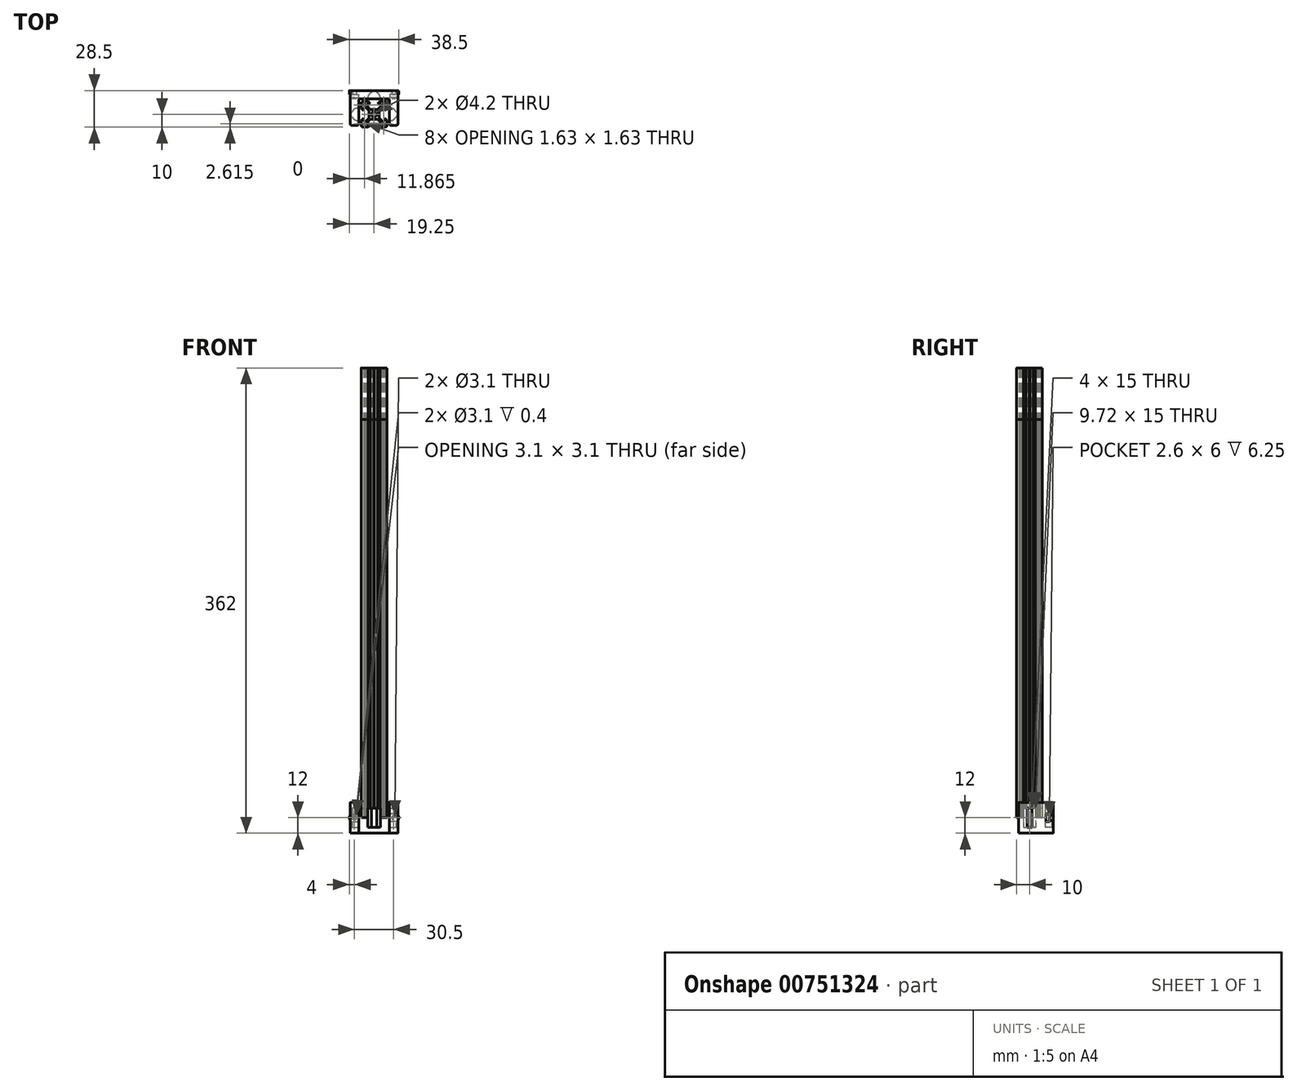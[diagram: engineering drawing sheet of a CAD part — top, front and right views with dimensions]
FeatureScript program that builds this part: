
annotation { "Feature Type Name" : "Feature", "Feature Type Description" : "" }
export const myFeature = defineFeature(function(context is Context, id is Id, definition is map)
    precondition{}
    {
        {
            var Q0;
            Q0=qCreatedBy(makeId("Top.planeOp"),FACE);
            var sketch = newSketch(context, id + "F0", { "sketchPlane" : qUnion([Q0])});
            skArc(sketch, "E0", {"start": v(-8.5, 10) * mm, "mid": v(-9.56, 9.56) * mm, "end": v(-10, 8.5) * mm});
            skLineSegment(sketch, "E1", {"start": v(-10, 8.5) * mm, "end": v(-10, 4.64) * mm});
            skLineSegment(sketch, "E2", {"start": v(-10, 4.64) * mm, "end": v(-8.2, 2.84) * mm});
            skLineSegment(sketch, "E3", {"start": v(-8.2, 5.5) * mm, "end": v(-8.2, 2.84) * mm});
            skLineSegment(sketch, "E4", {"start": v(-8.2, 5.5) * mm, "end": v(-6.56, 5.5) * mm});
            skLineSegment(sketch, "E5", {"start": v(-6.56, 5.5) * mm, "end": v(-3.9, 2.84) * mm});
            skLineSegment(sketch, "E6", {"start": v(-3.9, 2.84) * mm, "end": v(-3.9, 0.2) * mm});
            skLineSegment(sketch, "E7", {"start": v(-3.9, 0.2) * mm, "end": v(-3.7, 0) * mm});
            skLineSegment(sketch, "E8", {"start": v(-3.9, -0.2) * mm, "end": v(-3.7, 0) * mm});
            skLineSegment(sketch, "E9", {"start": v(-3.9, -2.84) * mm, "end": v(-3.9, -0.2) * mm});
            skLineSegment(sketch, "E10", {"start": v(-6.56, -5.5) * mm, "end": v(-3.9, -2.84) * mm});
            skLineSegment(sketch, "E11", {"start": v(-8.2, -5.5) * mm, "end": v(-6.56, -5.5) * mm});
            skLineSegment(sketch, "E12", {"start": v(-8.2, -5.5) * mm, "end": v(-8.2, -2.84) * mm});
            skLineSegment(sketch, "E13", {"start": v(-10, -4.64) * mm, "end": v(-8.2, -2.84) * mm});
            skLineSegment(sketch, "E14", {"start": v(-10, -8.5) * mm, "end": v(-10, -4.64) * mm});
            skArc(sketch, "E15", {"start": v(-10, -8.5) * mm, "mid": v(-9.56, -9.56) * mm, "end": v(-8.5, -10) * mm});
            skLineSegment(sketch, "E16", {"start": v(-8.5, -10) * mm, "end": v(-4.64, -10) * mm});
            skLineSegment(sketch, "E17", {"start": v(-4.64, -10) * mm, "end": v(-2.84, -8.2) * mm});
            skLineSegment(sketch, "E18", {"start": v(-2.84, -8.2) * mm, "end": v(-5.5, -8.2) * mm});
            skLineSegment(sketch, "E19", {"start": v(-5.5, -8.2) * mm, "end": v(-5.5, -6.56) * mm});
            skLineSegment(sketch, "E20", {"start": v(-5.5, -6.56) * mm, "end": v(-2.84, -3.9) * mm});
            skLineSegment(sketch, "E21", {"start": v(-0.2, -3.9) * mm, "end": v(-2.84, -3.9) * mm});
            skLineSegment(sketch, "E22", {"start": v(-0.2, -3.9) * mm, "end": v(0, -3.7) * mm});
            skLineSegment(sketch, "E23", {"start": v(0.2, -3.9) * mm, "end": v(0, -3.7) * mm});
            skLineSegment(sketch, "E24", {"start": v(0.2, -3.9) * mm, "end": v(2.84, -3.9) * mm});
            skLineSegment(sketch, "E25", {"start": v(5.5, -6.56) * mm, "end": v(2.84, -3.9) * mm});
            skLineSegment(sketch, "E26", {"start": v(5.5, -8.2) * mm, "end": v(5.5, -6.56) * mm});
            skLineSegment(sketch, "E27", {"start": v(2.84, -8.2) * mm, "end": v(5.5, -8.2) * mm});
            skLineSegment(sketch, "E28", {"start": v(4.64, -10) * mm, "end": v(2.84, -8.2) * mm});
            skLineSegment(sketch, "E29", {"start": v(8.5, -10) * mm, "end": v(4.64, -10) * mm});
            skArc(sketch, "E30", {"start": v(8.5, -10) * mm, "mid": v(9.56, -9.56) * mm, "end": v(10, -8.5) * mm});
            skLineSegment(sketch, "E31", {"start": v(10, -8.5) * mm, "end": v(10, -4.64) * mm});
            skLineSegment(sketch, "E32", {"start": v(10, -4.64) * mm, "end": v(8.2, -2.84) * mm});
            skLineSegment(sketch, "E33", {"start": v(8.2, -5.5) * mm, "end": v(8.2, -2.84) * mm});
            skLineSegment(sketch, "E34", {"start": v(8.2, -5.5) * mm, "end": v(6.56, -5.5) * mm});
            skLineSegment(sketch, "E35", {"start": v(6.56, -5.5) * mm, "end": v(3.9, -2.84) * mm});
            skLineSegment(sketch, "E36", {"start": v(3.9, -2.84) * mm, "end": v(3.9, -0.2) * mm});
            skLineSegment(sketch, "E37", {"start": v(3.9, -0.2) * mm, "end": v(3.7, 0) * mm});
            skLineSegment(sketch, "E38", {"start": v(3.9, 0.2) * mm, "end": v(3.7, 0) * mm});
            skLineSegment(sketch, "E39", {"start": v(3.9, 2.84) * mm, "end": v(3.9, 0.2) * mm});
            skLineSegment(sketch, "E40", {"start": v(6.56, 5.5) * mm, "end": v(3.9, 2.84) * mm});
            skLineSegment(sketch, "E41", {"start": v(8.2, 5.5) * mm, "end": v(6.56, 5.5) * mm});
            skLineSegment(sketch, "E42", {"start": v(8.2, 5.5) * mm, "end": v(8.2, 2.84) * mm});
            skLineSegment(sketch, "E43", {"start": v(10, 4.64) * mm, "end": v(8.2, 2.84) * mm});
            skLineSegment(sketch, "E44", {"start": v(10, 8.5) * mm, "end": v(10, 4.64) * mm});
            skArc(sketch, "E45", {"start": v(10, 8.5) * mm, "mid": v(9.56, 9.56) * mm, "end": v(8.5, 10) * mm});
            skLineSegment(sketch, "E46", {"start": v(8.5, 10) * mm, "end": v(4.64, 10) * mm});
            skLineSegment(sketch, "E47", {"start": v(4.64, 10) * mm, "end": v(2.84, 8.2) * mm});
            skLineSegment(sketch, "E48", {"start": v(2.84, 8.2) * mm, "end": v(5.5, 8.2) * mm});
            skLineSegment(sketch, "E49", {"start": v(5.5, 8.2) * mm, "end": v(5.5, 6.56) * mm});
            skLineSegment(sketch, "E50", {"start": v(5.5, 6.56) * mm, "end": v(2.84, 3.9) * mm});
            skLineSegment(sketch, "E51", {"start": v(0.2, 3.9) * mm, "end": v(2.84, 3.9) * mm});
            skLineSegment(sketch, "E52", {"start": v(0.2, 3.9) * mm, "end": v(0, 3.7) * mm});
            skLineSegment(sketch, "E53", {"start": v(-0.2, 3.9) * mm, "end": v(0, 3.7) * mm});
            skLineSegment(sketch, "E54", {"start": v(-0.2, 3.9) * mm, "end": v(-2.84, 3.9) * mm});
            skLineSegment(sketch, "E55", {"start": v(-5.5, 6.56) * mm, "end": v(-2.84, 3.9) * mm});
            skLineSegment(sketch, "E56", {"start": v(-5.5, 8.2) * mm, "end": v(-5.5, 6.56) * mm});
            skLineSegment(sketch, "E57", {"start": v(-2.84, 8.2) * mm, "end": v(-5.5, 8.2) * mm});
            skLineSegment(sketch, "E58", {"start": v(-4.64, 10) * mm, "end": v(-2.84, 8.2) * mm});
            skLineSegment(sketch, "E59", {"start": v(-8.5, 10) * mm, "end": v(-4.64, 10) * mm});
            skCircle(sketch, "E60", {"center": v(0, 0) * mm, "radius": 2.1 * mm});
            skLineSegment(sketch, "E61", {"start": v(-6.57, 8.2) * mm, "end": v(-8.2, 8.2) * mm});
            skLineSegment(sketch, "E62", {"start": v(-6.57, 8.2) * mm, "end": v(-6.57, 7.63) * mm});
            skLineSegment(sketch, "E63", {"start": v(-7.63, 6.57) * mm, "end": v(-6.57, 7.63) * mm});
            skLineSegment(sketch, "E64", {"start": v(-8.2, 6.57) * mm, "end": v(-7.63, 6.57) * mm});
            skLineSegment(sketch, "E65", {"start": v(-8.2, 8.2) * mm, "end": v(-8.2, 6.57) * mm});
            skLineSegment(sketch, "E66", {"start": v(8.2, 8.2) * mm, "end": v(8.2, 6.57) * mm});
            skLineSegment(sketch, "E67", {"start": v(8.2, 6.57) * mm, "end": v(7.63, 6.57) * mm});
            skLineSegment(sketch, "E68", {"start": v(7.63, 6.57) * mm, "end": v(6.57, 7.63) * mm});
            skLineSegment(sketch, "E69", {"start": v(6.57, 8.2) * mm, "end": v(6.57, 7.63) * mm});
            skLineSegment(sketch, "E70", {"start": v(6.57, 8.2) * mm, "end": v(8.2, 8.2) * mm});
            skLineSegment(sketch, "E71", {"start": v(-8.2, -8.2) * mm, "end": v(-8.2, -6.57) * mm});
            skLineSegment(sketch, "E72", {"start": v(-8.2, -6.57) * mm, "end": v(-7.63, -6.57) * mm});
            skLineSegment(sketch, "E73", {"start": v(-7.63, -6.57) * mm, "end": v(-6.57, -7.63) * mm});
            skLineSegment(sketch, "E74", {"start": v(-6.57, -8.2) * mm, "end": v(-6.57, -7.63) * mm});
            skLineSegment(sketch, "E75", {"start": v(-6.57, -8.2) * mm, "end": v(-8.2, -8.2) * mm});
            skLineSegment(sketch, "E76", {"start": v(6.57, -8.2) * mm, "end": v(8.2, -8.2) * mm});
            skLineSegment(sketch, "E77", {"start": v(6.57, -8.2) * mm, "end": v(6.57, -7.63) * mm});
            skLineSegment(sketch, "E78", {"start": v(7.63, -6.57) * mm, "end": v(6.57, -7.63) * mm});
            skLineSegment(sketch, "E79", {"start": v(8.2, -6.57) * mm, "end": v(7.63, -6.57) * mm});
            skLineSegment(sketch, "E80", {"start": v(8.2, -8.2) * mm, "end": v(8.2, -6.57) * mm});
            skSolve(sketch);
        }
        {
            var Q0;
            Q0 = qSketchRegion(id + "F0", true);
            extrude(context, id + "F1", {"entities" : qUnion([Q0]), "depth" : 310 * mm, "offsetDistance" : 25 * mm});
        }
        {
            var Q0;
            Q0 = qSketchRegion(id + "F0", true);
            extrude(context, id + "F2", {"entities" : qUnion([Q0]), "depth" : 350 * mm, "offsetDistance" : 25 * mm});
        }
        {
            var Q0;
            Q0=qCreatedBy(makeId("Top.planeOp"),FACE);
            var sketch = newSketch(context, id + "F3", { "sketchPlane" : qUnion([Q0])});
            skLineSegment(sketch, "E81.0.0", {"start": v(-4.64, 10) * mm, "end": v(-8.5, 10) * mm, "construction": true});
            skArc(sketch, "E81.0.1", {"start": v(-8.5, 10) * mm, "mid": v(-9.56, 9.56) * mm, "end": v(-10, 8.5) * mm, "construction": true});
            skLineSegment(sketch, "E81.0.2", {"start": v(-10, 8.5) * mm, "end": v(-10, 4.64) * mm, "construction": true});
            skLineSegment(sketch, "E81.0.3", {"start": v(-10, 4.64) * mm, "end": v(-8.2, 2.84) * mm, "construction": true});
            skLineSegment(sketch, "E81.0.4", {"start": v(-8.2, 2.84) * mm, "end": v(-8.2, 5.5) * mm, "construction": true});
            skLineSegment(sketch, "E81.0.5", {"start": v(-8.2, 5.5) * mm, "end": v(-6.56, 5.5) * mm, "construction": true});
            skLineSegment(sketch, "E81.0.6", {"start": v(-6.56, 5.5) * mm, "end": v(-3.9, 2.84) * mm, "construction": true});
            skLineSegment(sketch, "E81.0.7", {"start": v(-3.9, 2.84) * mm, "end": v(-3.9, 0.2) * mm, "construction": true});
            skLineSegment(sketch, "E81.0.8", {"start": v(-3.9, 0.2) * mm, "end": v(-3.7, 0) * mm, "construction": true});
            skLineSegment(sketch, "E81.0.9", {"start": v(-3.7, 0) * mm, "end": v(-3.9, -0.2) * mm, "construction": true});
            skLineSegment(sketch, "E81.0.10", {"start": v(-3.9, -0.2) * mm, "end": v(-3.9, -2.84) * mm, "construction": true});
            skLineSegment(sketch, "E81.0.11", {"start": v(-3.9, -2.84) * mm, "end": v(-6.56, -5.5) * mm, "construction": true});
            skLineSegment(sketch, "E81.0.12", {"start": v(-6.56, -5.5) * mm, "end": v(-8.2, -5.5) * mm, "construction": true});
            skLineSegment(sketch, "E81.0.13", {"start": v(-8.2, -5.5) * mm, "end": v(-8.2, -2.84) * mm, "construction": true});
            skLineSegment(sketch, "E81.0.14", {"start": v(-8.2, -2.84) * mm, "end": v(-10, -4.64) * mm, "construction": true});
            skLineSegment(sketch, "E81.0.15", {"start": v(-10, -4.64) * mm, "end": v(-10, -8.5) * mm, "construction": true});
            skArc(sketch, "E81.0.16", {"start": v(-10, -8.5) * mm, "mid": v(-9.56, -9.56) * mm, "end": v(-8.5, -10) * mm, "construction": true});
            skLineSegment(sketch, "E81.0.17", {"start": v(-8.5, -10) * mm, "end": v(-4.64, -10) * mm, "construction": true});
            skLineSegment(sketch, "E81.0.18", {"start": v(-4.64, -10) * mm, "end": v(-2.84, -8.2) * mm, "construction": true});
            skLineSegment(sketch, "E81.0.19", {"start": v(-2.84, -8.2) * mm, "end": v(-5.5, -8.2) * mm, "construction": true});
            skLineSegment(sketch, "E81.0.20", {"start": v(-5.5, -8.2) * mm, "end": v(-5.5, -6.56) * mm, "construction": true});
            skLineSegment(sketch, "E81.0.21", {"start": v(-5.5, -6.56) * mm, "end": v(-2.84, -3.9) * mm, "construction": true});
            skLineSegment(sketch, "E81.0.22", {"start": v(-2.84, -3.9) * mm, "end": v(-0.2, -3.9) * mm, "construction": true});
            skLineSegment(sketch, "E81.0.23", {"start": v(-0.2, -3.9) * mm, "end": v(0, -3.7) * mm, "construction": true});
            skLineSegment(sketch, "E81.0.24", {"start": v(0, -3.7) * mm, "end": v(0.2, -3.9) * mm, "construction": true});
            skLineSegment(sketch, "E81.0.25", {"start": v(0.2, -3.9) * mm, "end": v(2.84, -3.9) * mm, "construction": true});
            skLineSegment(sketch, "E81.0.26", {"start": v(2.84, -3.9) * mm, "end": v(5.5, -6.56) * mm, "construction": true});
            skLineSegment(sketch, "E81.0.27", {"start": v(5.5, -6.56) * mm, "end": v(5.5, -8.2) * mm, "construction": true});
            skLineSegment(sketch, "E81.0.28", {"start": v(5.5, -8.2) * mm, "end": v(2.84, -8.2) * mm, "construction": true});
            skLineSegment(sketch, "E81.0.29", {"start": v(2.84, -8.2) * mm, "end": v(4.64, -10) * mm, "construction": true});
            skLineSegment(sketch, "E81.0.30", {"start": v(4.64, -10) * mm, "end": v(8.5, -10) * mm, "construction": true});
            skArc(sketch, "E81.0.31", {"start": v(8.5, -10) * mm, "mid": v(9.56, -9.56) * mm, "end": v(10, -8.5) * mm, "construction": true});
            skLineSegment(sketch, "E81.0.32", {"start": v(10, -8.5) * mm, "end": v(10, -4.64) * mm, "construction": true});
            skLineSegment(sketch, "E81.0.33", {"start": v(10, -4.64) * mm, "end": v(8.2, -2.84) * mm, "construction": true});
            skLineSegment(sketch, "E81.0.34", {"start": v(8.2, -2.84) * mm, "end": v(8.2, -5.5) * mm, "construction": true});
            skLineSegment(sketch, "E81.0.35", {"start": v(8.2, -5.5) * mm, "end": v(6.56, -5.5) * mm, "construction": true});
            skLineSegment(sketch, "E81.0.36", {"start": v(6.56, -5.5) * mm, "end": v(3.9, -2.84) * mm, "construction": true});
            skLineSegment(sketch, "E81.0.37", {"start": v(3.9, -2.84) * mm, "end": v(3.9, -0.2) * mm, "construction": true});
            skLineSegment(sketch, "E81.0.38", {"start": v(3.9, -0.2) * mm, "end": v(3.7, 0) * mm, "construction": true});
            skLineSegment(sketch, "E81.0.39", {"start": v(3.7, 0) * mm, "end": v(3.9, 0.2) * mm, "construction": true});
            skLineSegment(sketch, "E81.0.40", {"start": v(3.9, 0.2) * mm, "end": v(3.9, 2.84) * mm, "construction": true});
            skLineSegment(sketch, "E81.0.41", {"start": v(3.9, 2.84) * mm, "end": v(6.56, 5.5) * mm, "construction": true});
            skLineSegment(sketch, "E81.0.42", {"start": v(6.56, 5.5) * mm, "end": v(8.2, 5.5) * mm, "construction": true});
            skLineSegment(sketch, "E81.0.43", {"start": v(8.2, 5.5) * mm, "end": v(8.2, 2.84) * mm, "construction": true});
            skLineSegment(sketch, "E81.0.44", {"start": v(8.2, 2.84) * mm, "end": v(10, 4.64) * mm, "construction": true});
            skLineSegment(sketch, "E81.0.45", {"start": v(10, 4.64) * mm, "end": v(10, 8.5) * mm, "construction": true});
            skArc(sketch, "E81.0.46", {"start": v(10, 8.5) * mm, "mid": v(9.56, 9.56) * mm, "end": v(8.5, 10) * mm, "construction": true});
            skLineSegment(sketch, "E81.0.47", {"start": v(8.5, 10) * mm, "end": v(4.64, 10) * mm, "construction": true});
            skLineSegment(sketch, "E81.0.48", {"start": v(4.64, 10) * mm, "end": v(2.84, 8.2) * mm, "construction": true});
            skLineSegment(sketch, "E81.0.49", {"start": v(2.84, 8.2) * mm, "end": v(5.5, 8.2) * mm, "construction": true});
            skLineSegment(sketch, "E81.0.50", {"start": v(5.5, 8.2) * mm, "end": v(5.5, 6.56) * mm, "construction": true});
            skLineSegment(sketch, "E81.0.51", {"start": v(5.5, 6.56) * mm, "end": v(2.84, 3.9) * mm, "construction": true});
            skLineSegment(sketch, "E81.0.52", {"start": v(2.84, 3.9) * mm, "end": v(0.2, 3.9) * mm, "construction": true});
            skLineSegment(sketch, "E81.0.53", {"start": v(0.2, 3.9) * mm, "end": v(0, 3.7) * mm, "construction": true});
            skLineSegment(sketch, "E81.0.54", {"start": v(0, 3.7) * mm, "end": v(-0.2, 3.9) * mm, "construction": true});
            skLineSegment(sketch, "E81.0.55", {"start": v(-0.2, 3.9) * mm, "end": v(-2.84, 3.9) * mm, "construction": true});
            skLineSegment(sketch, "E81.0.56", {"start": v(-2.84, 3.9) * mm, "end": v(-5.5, 6.56) * mm, "construction": true});
            skLineSegment(sketch, "E81.0.57", {"start": v(-5.5, 6.56) * mm, "end": v(-5.5, 8.2) * mm, "construction": true});
            skLineSegment(sketch, "E81.0.58", {"start": v(-5.5, 8.2) * mm, "end": v(-2.84, 8.2) * mm, "construction": true});
            skLineSegment(sketch, "E81.0.59", {"start": v(-2.84, 8.2) * mm, "end": v(-4.64, 10) * mm, "construction": true});
            skLineSegment(sketch, "E82.0.0", {"start": v(-6.57, 8.2) * mm, "end": v(-8.2, 8.2) * mm, "construction": true});
            skLineSegment(sketch, "E82.0.1", {"start": v(-8.2, 8.2) * mm, "end": v(-8.2, 6.57) * mm, "construction": true});
            skLineSegment(sketch, "E82.0.2", {"start": v(-8.2, 6.57) * mm, "end": v(-7.63, 6.57) * mm, "construction": true});
            skLineSegment(sketch, "E82.0.3", {"start": v(-7.63, 6.57) * mm, "end": v(-6.57, 7.63) * mm, "construction": true});
            skLineSegment(sketch, "E82.0.4", {"start": v(-6.57, 7.63) * mm, "end": v(-6.57, 8.2) * mm, "construction": true});
            skLineSegment(sketch, "E83.0.0", {"start": v(8.2, 8.2) * mm, "end": v(6.57, 8.2) * mm, "construction": true});
            skLineSegment(sketch, "E83.0.1", {"start": v(6.57, 8.2) * mm, "end": v(6.57, 7.63) * mm, "construction": true});
            skLineSegment(sketch, "E83.0.2", {"start": v(6.57, 7.63) * mm, "end": v(7.63, 6.57) * mm, "construction": true});
            skLineSegment(sketch, "E83.0.3", {"start": v(7.63, 6.57) * mm, "end": v(8.2, 6.57) * mm, "construction": true});
            skLineSegment(sketch, "E83.0.4", {"start": v(8.2, 6.57) * mm, "end": v(8.2, 8.2) * mm, "construction": true});
            skLineSegment(sketch, "E84.0.0", {"start": v(-8.2, -8.2) * mm, "end": v(-6.57, -8.2) * mm, "construction": true});
            skLineSegment(sketch, "E84.0.1", {"start": v(-6.57, -8.2) * mm, "end": v(-6.57, -7.63) * mm, "construction": true});
            skLineSegment(sketch, "E84.0.2", {"start": v(-6.57, -7.63) * mm, "end": v(-7.63, -6.57) * mm, "construction": true});
            skLineSegment(sketch, "E84.0.3", {"start": v(-7.63, -6.57) * mm, "end": v(-8.2, -6.57) * mm, "construction": true});
            skLineSegment(sketch, "E84.0.4", {"start": v(-8.2, -6.57) * mm, "end": v(-8.2, -8.2) * mm, "construction": true});
            skLineSegment(sketch, "E85.0.0", {"start": v(6.57, -8.2) * mm, "end": v(8.2, -8.2) * mm, "construction": true});
            skLineSegment(sketch, "E85.0.1", {"start": v(8.2, -8.2) * mm, "end": v(8.2, -6.57) * mm, "construction": true});
            skLineSegment(sketch, "E85.0.2", {"start": v(8.2, -6.57) * mm, "end": v(7.63, -6.57) * mm, "construction": true});
            skLineSegment(sketch, "E85.0.3", {"start": v(7.63, -6.57) * mm, "end": v(6.57, -7.63) * mm, "construction": true});
            skLineSegment(sketch, "E85.0.4", {"start": v(6.57, -7.63) * mm, "end": v(6.57, -8.2) * mm, "construction": true});
            skCircle(sketch, "E86.0", {"center": v(0, 0) * mm, "radius": 2.1 * mm, "construction": true});
            skCircle(sketch, "E87", {"center": v(0, 12.1) * mm, "radius": 4.76 * mm});
            skCircle(sketch, "E88", {"center": v(-12.1, 0) * mm, "radius": 4.76 * mm});
            skCircle(sketch, "E89", {"center": v(12.1, 0) * mm, "radius": 4.76 * mm});
            skSolve(sketch);
        }
        {
            var Q0;
            Q0=qCreatedBy(makeId("Top.planeOp"),FACE);
            var sketch = newSketch(context, id + "F4", { "sketchPlane" : qUnion([Q0])});
            skLineSegment(sketch, "E90.0.0", {"start": v(-4.64, 10) * mm, "end": v(-8.5, 10) * mm, "construction": true});
            skArc(sketch, "E90.0.1", {"start": v(-8.5, 10) * mm, "mid": v(-9.56, 9.56) * mm, "end": v(-10, 8.5) * mm, "construction": true});
            skLineSegment(sketch, "E90.0.2", {"start": v(-10, 8.5) * mm, "end": v(-10, 4.64) * mm, "construction": true});
            skLineSegment(sketch, "E90.0.3", {"start": v(-10, 4.64) * mm, "end": v(-8.2, 2.84) * mm, "construction": true});
            skLineSegment(sketch, "E90.0.4", {"start": v(-8.2, 2.84) * mm, "end": v(-8.2, 5.5) * mm, "construction": true});
            skLineSegment(sketch, "E90.0.5", {"start": v(-8.2, 5.5) * mm, "end": v(-6.56, 5.5) * mm, "construction": true});
            skLineSegment(sketch, "E90.0.6", {"start": v(-6.56, 5.5) * mm, "end": v(-3.9, 2.84) * mm, "construction": true});
            skLineSegment(sketch, "E90.0.7", {"start": v(-3.9, 2.84) * mm, "end": v(-3.9, 0.2) * mm, "construction": true});
            skLineSegment(sketch, "E90.0.8", {"start": v(-3.9, 0.2) * mm, "end": v(-3.7, 0) * mm, "construction": true});
            skLineSegment(sketch, "E90.0.9", {"start": v(-3.7, 0) * mm, "end": v(-3.9, -0.2) * mm, "construction": true});
            skLineSegment(sketch, "E90.0.10", {"start": v(-3.9, -0.2) * mm, "end": v(-3.9, -2.84) * mm, "construction": true});
            skLineSegment(sketch, "E90.0.11", {"start": v(-3.9, -2.84) * mm, "end": v(-6.56, -5.5) * mm, "construction": true});
            skLineSegment(sketch, "E90.0.12", {"start": v(-6.56, -5.5) * mm, "end": v(-8.2, -5.5) * mm, "construction": true});
            skLineSegment(sketch, "E90.0.13", {"start": v(-8.2, -5.5) * mm, "end": v(-8.2, -2.84) * mm, "construction": true});
            skLineSegment(sketch, "E90.0.14", {"start": v(-8.2, -2.84) * mm, "end": v(-10, -4.64) * mm, "construction": true});
            skLineSegment(sketch, "E90.0.15", {"start": v(-10, -4.64) * mm, "end": v(-10, -8.5) * mm, "construction": true});
            skArc(sketch, "E90.0.16", {"start": v(-10, -8.5) * mm, "mid": v(-9.56, -9.56) * mm, "end": v(-8.5, -10) * mm, "construction": true});
            skLineSegment(sketch, "E90.0.17", {"start": v(-8.5, -10) * mm, "end": v(-4.64, -10) * mm, "construction": true});
            skLineSegment(sketch, "E90.0.18", {"start": v(-4.64, -10) * mm, "end": v(-2.84, -8.2) * mm, "construction": true});
            skLineSegment(sketch, "E90.0.19", {"start": v(-2.84, -8.2) * mm, "end": v(-5.5, -8.2) * mm, "construction": true});
            skLineSegment(sketch, "E90.0.20", {"start": v(-5.5, -8.2) * mm, "end": v(-5.5, -6.56) * mm, "construction": true});
            skLineSegment(sketch, "E90.0.21", {"start": v(-5.5, -6.56) * mm, "end": v(-2.84, -3.9) * mm, "construction": true});
            skLineSegment(sketch, "E90.0.22", {"start": v(-2.84, -3.9) * mm, "end": v(-0.2, -3.9) * mm, "construction": true});
            skLineSegment(sketch, "E90.0.23", {"start": v(-0.2, -3.9) * mm, "end": v(0, -3.7) * mm, "construction": true});
            skLineSegment(sketch, "E90.0.24", {"start": v(0, -3.7) * mm, "end": v(0.2, -3.9) * mm, "construction": true});
            skLineSegment(sketch, "E90.0.25", {"start": v(0.2, -3.9) * mm, "end": v(2.84, -3.9) * mm, "construction": true});
            skLineSegment(sketch, "E90.0.26", {"start": v(2.84, -3.9) * mm, "end": v(5.5, -6.56) * mm, "construction": true});
            skLineSegment(sketch, "E90.0.27", {"start": v(5.5, -6.56) * mm, "end": v(5.5, -8.2) * mm, "construction": true});
            skLineSegment(sketch, "E90.0.28", {"start": v(5.5, -8.2) * mm, "end": v(2.84, -8.2) * mm, "construction": true});
            skLineSegment(sketch, "E90.0.29", {"start": v(2.84, -8.2) * mm, "end": v(4.64, -10) * mm, "construction": true});
            skLineSegment(sketch, "E90.0.30", {"start": v(4.64, -10) * mm, "end": v(8.5, -10) * mm, "construction": true});
            skArc(sketch, "E90.0.31", {"start": v(8.5, -10) * mm, "mid": v(9.56, -9.56) * mm, "end": v(10, -8.5) * mm, "construction": true});
            skLineSegment(sketch, "E90.0.32", {"start": v(10, -8.5) * mm, "end": v(10, -4.64) * mm, "construction": true});
            skLineSegment(sketch, "E90.0.33", {"start": v(10, -4.64) * mm, "end": v(8.2, -2.84) * mm, "construction": true});
            skLineSegment(sketch, "E90.0.34", {"start": v(8.2, -2.84) * mm, "end": v(8.2, -5.5) * mm, "construction": true});
            skLineSegment(sketch, "E90.0.35", {"start": v(8.2, -5.5) * mm, "end": v(6.56, -5.5) * mm, "construction": true});
            skLineSegment(sketch, "E90.0.36", {"start": v(6.56, -5.5) * mm, "end": v(3.9, -2.84) * mm, "construction": true});
            skLineSegment(sketch, "E90.0.37", {"start": v(3.9, -2.84) * mm, "end": v(3.9, -0.2) * mm, "construction": true});
            skLineSegment(sketch, "E90.0.38", {"start": v(3.9, -0.2) * mm, "end": v(3.7, 0) * mm, "construction": true});
            skLineSegment(sketch, "E90.0.39", {"start": v(3.7, 0) * mm, "end": v(3.9, 0.2) * mm, "construction": true});
            skLineSegment(sketch, "E90.0.40", {"start": v(3.9, 0.2) * mm, "end": v(3.9, 2.84) * mm, "construction": true});
            skLineSegment(sketch, "E90.0.41", {"start": v(3.9, 2.84) * mm, "end": v(6.56, 5.5) * mm, "construction": true});
            skLineSegment(sketch, "E90.0.42", {"start": v(6.56, 5.5) * mm, "end": v(8.2, 5.5) * mm, "construction": true});
            skLineSegment(sketch, "E90.0.43", {"start": v(8.2, 5.5) * mm, "end": v(8.2, 2.84) * mm, "construction": true});
            skLineSegment(sketch, "E90.0.44", {"start": v(8.2, 2.84) * mm, "end": v(10, 4.64) * mm, "construction": true});
            skLineSegment(sketch, "E90.0.45", {"start": v(10, 4.64) * mm, "end": v(10, 8.5) * mm, "construction": true});
            skArc(sketch, "E90.0.46", {"start": v(10, 8.5) * mm, "mid": v(9.56, 9.56) * mm, "end": v(8.5, 10) * mm, "construction": true});
            skLineSegment(sketch, "E90.0.47", {"start": v(8.5, 10) * mm, "end": v(4.64, 10) * mm, "construction": true});
            skLineSegment(sketch, "E90.0.48", {"start": v(4.64, 10) * mm, "end": v(2.84, 8.2) * mm, "construction": true});
            skLineSegment(sketch, "E90.0.49", {"start": v(2.84, 8.2) * mm, "end": v(5.5, 8.2) * mm, "construction": true});
            skLineSegment(sketch, "E90.0.50", {"start": v(5.5, 8.2) * mm, "end": v(5.5, 6.56) * mm, "construction": true});
            skLineSegment(sketch, "E90.0.51", {"start": v(5.5, 6.56) * mm, "end": v(2.84, 3.9) * mm, "construction": true});
            skLineSegment(sketch, "E90.0.52", {"start": v(2.84, 3.9) * mm, "end": v(0.2, 3.9) * mm, "construction": true});
            skLineSegment(sketch, "E90.0.53", {"start": v(0.2, 3.9) * mm, "end": v(0, 3.7) * mm, "construction": true});
            skLineSegment(sketch, "E90.0.54", {"start": v(0, 3.7) * mm, "end": v(-0.2, 3.9) * mm, "construction": true});
            skLineSegment(sketch, "E90.0.55", {"start": v(-0.2, 3.9) * mm, "end": v(-2.84, 3.9) * mm, "construction": true});
            skLineSegment(sketch, "E90.0.56", {"start": v(-2.84, 3.9) * mm, "end": v(-5.5, 6.56) * mm, "construction": true});
            skLineSegment(sketch, "E90.0.57", {"start": v(-5.5, 6.56) * mm, "end": v(-5.5, 8.2) * mm, "construction": true});
            skLineSegment(sketch, "E90.0.58", {"start": v(-5.5, 8.2) * mm, "end": v(-2.84, 8.2) * mm, "construction": true});
            skLineSegment(sketch, "E90.0.59", {"start": v(-2.84, 8.2) * mm, "end": v(-4.64, 10) * mm, "construction": true});
            skCircle(sketch, "E91.0.0", {"center": v(0, 0) * mm, "radius": 2.1 * mm, "construction": true});
            skLineSegment(sketch, "E92.0.0", {"start": v(-6.57, 8.2) * mm, "end": v(-8.2, 8.2) * mm, "construction": true});
            skLineSegment(sketch, "E92.0.1", {"start": v(-8.2, 8.2) * mm, "end": v(-8.2, 6.57) * mm, "construction": true});
            skLineSegment(sketch, "E92.0.2", {"start": v(-8.2, 6.57) * mm, "end": v(-7.63, 6.57) * mm, "construction": true});
            skLineSegment(sketch, "E92.0.3", {"start": v(-7.63, 6.57) * mm, "end": v(-6.57, 7.63) * mm, "construction": true});
            skLineSegment(sketch, "E92.0.4", {"start": v(-6.57, 7.63) * mm, "end": v(-6.57, 8.2) * mm, "construction": true});
            skLineSegment(sketch, "E93.0.0", {"start": v(8.2, 8.2) * mm, "end": v(6.57, 8.2) * mm, "construction": true});
            skLineSegment(sketch, "E93.0.1", {"start": v(6.57, 8.2) * mm, "end": v(6.57, 7.63) * mm, "construction": true});
            skLineSegment(sketch, "E93.0.2", {"start": v(6.57, 7.63) * mm, "end": v(7.63, 6.57) * mm, "construction": true});
            skLineSegment(sketch, "E93.0.3", {"start": v(7.63, 6.57) * mm, "end": v(8.2, 6.57) * mm, "construction": true});
            skLineSegment(sketch, "E93.0.4", {"start": v(8.2, 6.57) * mm, "end": v(8.2, 8.2) * mm, "construction": true});
            skLineSegment(sketch, "E94.0.0", {"start": v(-8.2, -8.2) * mm, "end": v(-6.57, -8.2) * mm, "construction": true});
            skLineSegment(sketch, "E94.0.1", {"start": v(-6.57, -8.2) * mm, "end": v(-6.57, -7.63) * mm, "construction": true});
            skLineSegment(sketch, "E94.0.2", {"start": v(-6.57, -7.63) * mm, "end": v(-7.63, -6.57) * mm, "construction": true});
            skLineSegment(sketch, "E94.0.3", {"start": v(-7.63, -6.57) * mm, "end": v(-8.2, -6.57) * mm, "construction": true});
            skLineSegment(sketch, "E94.0.4", {"start": v(-8.2, -6.57) * mm, "end": v(-8.2, -8.2) * mm, "construction": true});
            skLineSegment(sketch, "E95.0.0", {"start": v(6.57, -8.2) * mm, "end": v(8.2, -8.2) * mm, "construction": true});
            skLineSegment(sketch, "E95.0.1", {"start": v(8.2, -8.2) * mm, "end": v(8.2, -6.57) * mm, "construction": true});
            skLineSegment(sketch, "E95.0.2", {"start": v(8.2, -6.57) * mm, "end": v(7.63, -6.57) * mm, "construction": true});
            skLineSegment(sketch, "E95.0.3", {"start": v(7.63, -6.57) * mm, "end": v(6.57, -7.63) * mm, "construction": true});
            skLineSegment(sketch, "E95.0.4", {"start": v(6.57, -7.63) * mm, "end": v(6.57, -8.2) * mm, "construction": true});
            skLineSegment(sketch, "E96", {"start": v(-18.5, 18.5) * mm, "end": v(18.5, 18.5) * mm});
            skLineSegment(sketch, "E97", {"start": v(-18.5, 18.5) * mm, "end": v(-18.5, -8.5) * mm});
            skLineSegment(sketch, "E98", {"start": v(-18.5, -8.5) * mm, "end": v(-12, -8.5) * mm});
            skLineSegment(sketch, "E99", {"start": v(-12, -8.5) * mm, "end": v(-12, 12) * mm});
            skLineSegment(sketch, "E100", {"start": v(-12, 12) * mm, "end": v(12, 12) * mm});
            skLineSegment(sketch, "E101", {"start": v(12, 12) * mm, "end": v(12, -8.5) * mm});
            skLineSegment(sketch, "E102", {"start": v(12, -8.5) * mm, "end": v(18.5, -8.5) * mm});
            skLineSegment(sketch, "E103", {"start": v(18.5, -8.5) * mm, "end": v(18.5, 18.5) * mm});
            skSolve(sketch);
        }
        {
            var Q0;
            Q0=qCreatedBy(makeId("Top.planeOp"),FACE);
            var sketch = newSketch(context, id + "F5", { "sketchPlane" : qUnion([Q0])});
            skCircle(sketch, "E104.0.0", {"center": v(-12.1, 0) * mm, "radius": 4.76 * mm, "construction": true});
            skCircle(sketch, "E105.0.0", {"center": v(0, 12.1) * mm, "radius": 4.76 * mm, "construction": true});
            skCircle(sketch, "E105.1.0", {"center": v(12.1, 0) * mm, "radius": 4.76 * mm, "construction": true});
            skLineSegment(sketch, "E106", {"start": v(-12.1, 0) * mm, "end": v(12.1, 0) * mm});
            skLineSegment(sketch, "E107", {"start": v(0, 12.1) * mm, "end": v(0, -10.5) * mm});
            skArc(sketch, "E108.0.startCap", {"start": v(-12.65, -4.86) * mm, "mid": v(-17.5, 0) * mm, "end": v(-12.65, 4.86) * mm});
            skArc(sketch, "E108.0.endCap", {"start": v(12.65, 4.86) * mm, "mid": v(17.5, 0) * mm, "end": v(12.65, -4.86) * mm});
            skLineSegment(sketch, "E108.0.left", {"start": v(-12.65, 4.86) * mm, "end": v(-4.86, 4.86) * mm});
            skLineSegment(sketch, "E108.0.right", {"start": v(-12.65, -4.86) * mm, "end": v(-4.86, -4.86) * mm});
            skArc(sketch, "E109.0.startCap", {"start": v(-4.86, 12.65) * mm, "mid": v(0, 17.5) * mm, "end": v(4.86, 12.65) * mm});
            skArc(sketch, "E109.0.endCap", {"start": v(4.86, -10.5) * mm, "mid": v(0, -15.36) * mm, "end": v(-4.86, -10.5) * mm});
            skLineSegment(sketch, "E109.0.left", {"start": v(4.86, 12.65) * mm, "end": v(4.86, 4.86) * mm});
            skLineSegment(sketch, "E109.0.right", {"start": v(-4.86, 12.65) * mm, "end": v(-4.86, 4.86) * mm});
            skLineSegment(sketch, "E110.bottom", {"start": v(-24.72, 2) * mm, "end": v(-12.1, 2) * mm});
            skLineSegment(sketch, "E110.top", {"start": v(-24.72, -2) * mm, "end": v(-12.1, -2) * mm});
            skLineSegment(sketch, "E110.left", {"start": v(-24.72, 2) * mm, "end": v(-24.72, -2) * mm});
            skLineSegment(sketch, "E110.right", {"start": v(-12.1, 2) * mm, "end": v(-12.1, -2) * mm, "construction": true});
            skLineSegment(sketch, "E111.MirrorCS", {"start": v(24.72, 2) * mm, "end": v(12.1, 2) * mm});
            skLineSegment(sketch, "E112.MirrorCS", {"start": v(24.72, -2) * mm, "end": v(12.1, -2) * mm});
            skLineSegment(sketch, "E113.MirrorCS", {"start": v(24.72, 2) * mm, "end": v(24.72, -2) * mm});
            skLineSegment(sketch, "E114.bottom", {"start": v(-2, 25.26) * mm, "end": v(2, 25.26) * mm});
            skLineSegment(sketch, "E114.top", {"start": v(-2, 12.1) * mm, "end": v(2, 12.1) * mm, "construction": true});
            skLineSegment(sketch, "E114.left", {"start": v(-2, 25.26) * mm, "end": v(-2, 12.1) * mm});
            skLineSegment(sketch, "E114.right", {"start": v(2, 25.26) * mm, "end": v(2, 12.1) * mm});
            skLineSegment(sketch, "E115.trimOffspring", {"start": v(-4.86, -4.86) * mm, "end": v(-4.86, -10.5) * mm});
            skLineSegment(sketch, "E116.trimOffspring", {"start": v(4.86, 4.86) * mm, "end": v(12.65, 4.86) * mm});
            skLineSegment(sketch, "E117.trimOffspring", {"start": v(4.86, -4.86) * mm, "end": v(4.86, -10.5) * mm});
            skLineSegment(sketch, "E118.trimOffspring", {"start": v(4.86, -4.86) * mm, "end": v(12.65, -4.86) * mm});
            skSolve(sketch);
        }
        {
            var Q0;
            Q0=qCreatedBy(makeId("Top.planeOp"),FACE);
            var sketch = newSketch(context, id + "F6", { "sketchPlane" : qUnion([Q0])});
            skLineSegment(sketch, "E119.0.0", {"start": v(12, -8.5) * mm, "end": v(18.5, -8.5) * mm, "construction": true});
            skLineSegment(sketch, "E119.0.1", {"start": v(18.5, -8.5) * mm, "end": v(18.5, 18.5) * mm, "construction": true});
            skLineSegment(sketch, "E119.0.2", {"start": v(18.5, 18.5) * mm, "end": v(-18.5, 18.5) * mm, "construction": true});
            skLineSegment(sketch, "E119.0.3", {"start": v(-18.5, 18.5) * mm, "end": v(-18.5, -8.5) * mm, "construction": true});
            skLineSegment(sketch, "E119.0.4", {"start": v(-18.5, -8.5) * mm, "end": v(-12, -8.5) * mm, "construction": true});
            skLineSegment(sketch, "E119.0.5", {"start": v(-12, -8.5) * mm, "end": v(-12, 12) * mm, "construction": true});
            skLineSegment(sketch, "E119.0.6", {"start": v(-12, 12) * mm, "end": v(12, 12) * mm, "construction": true});
            skLineSegment(sketch, "E119.0.7", {"start": v(12, 12) * mm, "end": v(12, -8.5) * mm, "construction": true});
            skPoint(sketch, "E120.firstSnap0", {"position": v(-15.25, -8.5) * mm});
            skLineSegment(sketch, "E120.bottom", {"start": v(-15.25, 18.5) * mm, "end": v(-16.8, 18.5) * mm});
            skLineSegment(sketch, "E120.top", {"start": v(-15.25, 12.5) * mm, "end": v(-16.8, 12.5) * mm});
            skLineSegment(sketch, "E120.left", {"start": v(-15.25, 18.5) * mm, "end": v(-15.25, 12.5) * mm});
            skLineSegment(sketch, "E120.right", {"start": v(-16.8, 18.5) * mm, "end": v(-16.8, 12.5) * mm});
            skPoint(sketch, "E121", {"position": v(15.25, -8.5) * mm});
            skLineSegment(sketch, "E122.MirrorCS", {"start": v(15.25, 18.5) * mm, "end": v(15.25, 12.5) * mm});
            skLineSegment(sketch, "E123.MirrorCS", {"start": v(16.8, 18.5) * mm, "end": v(16.8, 12.5) * mm});
            skLineSegment(sketch, "E124.MirrorCS", {"start": v(15.25, 12.5) * mm, "end": v(16.8, 12.5) * mm});
            skLineSegment(sketch, "E125.MirrorCS", {"start": v(15.25, 18.5) * mm, "end": v(16.8, 18.5) * mm});
            skSolve(sketch);
        }
        {
            var Q0;
            Q0=qCreatedBy(makeId("Top.planeOp"),FACE);
            var sketch = newSketch(context, id + "F7", { "sketchPlane" : qUnion([Q0])});
            skLineSegment(sketch, "E126.0.0", {"start": v(12, -8.5) * mm, "end": v(18.5, -8.5) * mm, "construction": true});
            skLineSegment(sketch, "E126.0.1", {"start": v(18.5, -8.5) * mm, "end": v(18.5, 18.5) * mm, "construction": true});
            skLineSegment(sketch, "E126.0.2", {"start": v(18.5, 18.5) * mm, "end": v(-18.5, 18.5) * mm, "construction": true});
            skLineSegment(sketch, "E126.0.3", {"start": v(-18.5, 18.5) * mm, "end": v(-18.5, -8.5) * mm, "construction": true});
            skLineSegment(sketch, "E126.0.4", {"start": v(-18.5, -8.5) * mm, "end": v(-12, -8.5) * mm, "construction": true});
            skLineSegment(sketch, "E126.0.5", {"start": v(-12, -8.5) * mm, "end": v(-12, 12) * mm, "construction": true});
            skLineSegment(sketch, "E126.0.6", {"start": v(-12, 12) * mm, "end": v(12, 12) * mm, "construction": true});
            skLineSegment(sketch, "E126.0.7", {"start": v(12, 12) * mm, "end": v(12, -8.5) * mm, "construction": true});
            skPoint(sketch, "E127.0", {"position": v(-15.25, 18.5) * mm});
            skLineSegment(sketch, "E128.bottom", {"start": v(-18.5, 15.5) * mm, "end": v(-12.25, 15.5) * mm});
            skLineSegment(sketch, "E128.top", {"start": v(-18.5, 12.9) * mm, "end": v(-12.25, 12.9) * mm});
            skLineSegment(sketch, "E128.left", {"start": v(-18.5, 15.5) * mm, "end": v(-18.5, 12.9) * mm});
            skLineSegment(sketch, "E128.right", {"start": v(-12.25, 15.5) * mm, "end": v(-12.25, 12.9) * mm});
            skLineSegment(sketch, "E129.MirrorCS", {"start": v(12.25, 15.5) * mm, "end": v(12.25, 12.9) * mm});
            skLineSegment(sketch, "E130.MirrorCS", {"start": v(18.5, 15.5) * mm, "end": v(12.25, 15.5) * mm});
            skLineSegment(sketch, "E131.MirrorCS", {"start": v(18.5, 12.9) * mm, "end": v(12.25, 12.9) * mm});
            skLineSegment(sketch, "E132.MirrorCS", {"start": v(18.5, 15.5) * mm, "end": v(18.5, 12.9) * mm});
            skSolve(sketch);
        }
        {
            var Q0;
            Q0 = qSketchRegion(id + "F4", true);
            extrude(context, id + "F8", {"entities" : qUnion([Q0]), "depth" : 24 * mm, "offsetDistance" : 25 * mm, "symmetric" : true});
        }
        {
            var Q0;
            Q0 = qSketchRegion(id + "F5", true);
            extrude(context, id + "F9", {"entities" : qUnion([Q0]), "operationType" : NewBodyOperationType.REMOVE, "depth" : 15 * mm, "offsetDistance" : 25 * mm, "symmetric" : true});
        }
        {
            var Q0;
            Q0=makeQuery(id+"F8.opExtrude","SWEPT_FACE",FACE,{"disambiguationData":[OSD([sQuery(id+"F4.wireOp",EDGE,"E96")])]});
            var sketch = newSketch(context, id + "F10", { "sketchPlane" : qUnion([Q0])});
            skPoint(sketch, "E133.0", {"position": v(-15.25, 0) * mm});
            skPoint(sketch, "E134.0", {"position": v(15.25, 0) * mm});
            skCircle(sketch, "E135", {"center": v(-15.25, 0) * mm, "radius": 4 * mm});
            skCircle(sketch, "E136.MirrorC", {"center": v(15.25, 0) * mm, "radius": 4 * mm});
            skSolve(sketch);
        }
        {
            var Q0;
            Q0 = qSketchRegion(id + "F10", true);
            extrude(context, id + "F11", {"entities" : qUnion([Q0]), "operationType" : NewBodyOperationType.ADD, "oppositeDirection" : true, "depth" : 3 * mm, "offsetDistance" : 25 * mm});
        }
        {
            var Q0;
            Q0=makeQuery(id+"F6.imprint","IMPRINT",FACE,{"disambiguationData":[TD([[makeQuery(id+"F6.imprint","IMPRINT",EDGE,{"derivedFrom":sQuery(id+"F6.wireOp",EDGE,"E120.bottom")}),1.0]])]});
            var Q1;
            Q1=sQuery(id+"F6.wireOp",EDGE,"E120.left");
            revolve(context, id + "F12", {"operationType" : NewBodyOperationType.REMOVE, "surfaceOperationType" : NewSurfaceOperationType.NEW, "entities" : qUnion([Q0]), "axis" : qUnion([Q1]), "revolveType" : RevolveType.FULL, "oppositeDirection" : true});
        }
        {
            var Q0;
            Q0=makeQuery(id+"F6.imprint","IMPRINT",FACE,{"disambiguationData":[TD([[makeQuery(id+"F6.imprint","IMPRINT",EDGE,{"derivedFrom":sQuery(id+"F6.wireOp",EDGE,"E122.MirrorCS")}),1.0]])]});
            var Q1;
            Q1=sQuery(id+"F6.wireOp",EDGE,"E122.MirrorCS");
            revolve(context, id + "F13", {"operationType" : NewBodyOperationType.REMOVE, "surfaceOperationType" : NewSurfaceOperationType.NEW, "entities" : qUnion([Q0]), "axis" : qUnion([Q1]), "revolveType" : RevolveType.FULL, "oppositeDirection" : true});
        }
        {
            var Q0;
            Q0 = qSketchRegion(id + "F7", true);
            extrude(context, id + "F14", {"entities" : qUnion([Q0]), "operationType" : NewBodyOperationType.REMOVE, "depth" : 6 * mm, "offsetDistance" : 25 * mm, "symmetric" : true});
        }
        {
            var Q0;
            Q0=makeQuery(id+"F8.opExtrude","SWEPT_EDGE",EDGE,{"disambiguationData":[OSD([sQuery(id+"F4.wireOp",EDGE,"E96"),sQuery(id+"F4.wireOp",EDGE,"E97")])]});
            var Q1;
            Q1=makeQuery(id+"F8.opExtrude","SWEPT_EDGE",EDGE,{"disambiguationData":[OSD([sQuery(id+"F4.wireOp",EDGE,"E97"),sQuery(id+"F4.wireOp",EDGE,"E98")])]});
            var Q2;
            Q2=makeQuery(id+"F8.opExtrude","SWEPT_EDGE",EDGE,{"disambiguationData":[OSD([sQuery(id+"F4.wireOp",EDGE,"E98"),sQuery(id+"F4.wireOp",EDGE,"E99")])]});
            var Q3;
            Q3=makeQuery(id+"F8.opExtrude","SWEPT_EDGE",EDGE,{"disambiguationData":[OSD([sQuery(id+"F4.wireOp",EDGE,"E101"),sQuery(id+"F4.wireOp",EDGE,"E102")])]});
            var Q4;
            Q4=makeQuery(id+"F8.opExtrude","SWEPT_EDGE",EDGE,{"disambiguationData":[OSD([sQuery(id+"F4.wireOp",EDGE,"E102"),sQuery(id+"F4.wireOp",EDGE,"E103")])]});
            var Q5;
            Q5=makeQuery(id+"F8.opExtrude","SWEPT_EDGE",EDGE,{"disambiguationData":[OSD([sQuery(id+"F4.wireOp",EDGE,"E100"),sQuery(id+"F4.wireOp",EDGE,"E101")])]});
            var Q6;
            Q6=makeQuery(id+"F8.opExtrude","SWEPT_EDGE",EDGE,{"disambiguationData":[OSD([sQuery(id+"F4.wireOp",EDGE,"E99"),sQuery(id+"F4.wireOp",EDGE,"E100")])]});
            var Q7;
            Q7=makeQuery(id+"F8.opExtrude","SWEPT_EDGE",EDGE,{"disambiguationData":[OSD([sQuery(id+"F4.wireOp",EDGE,"E96"),sQuery(id+"F4.wireOp",EDGE,"E103")])]});
            fillet(context, id + "F15", {"entities" : qUnion([Q0, Q1, Q2, Q3, Q4, Q5, Q6, Q7]), "radius" : 1 * mm, "allowEdgeOverflow" : false});
        }
        {
            var Q0;
            Q0=makeQuery(id+"F8.opExtrude","CAP_FACE",FACE,{"disambiguationData":[OSD([sQuery(id+"F4.wireOp",EDGE,"E96"),sQuery(id+"F4.wireOp",EDGE,"E97"),sQuery(id+"F4.wireOp",EDGE,"E98"),sQuery(id+"F4.wireOp",EDGE,"E99"),sQuery(id+"F4.wireOp",EDGE,"E100"),sQuery(id+"F4.wireOp",EDGE,"E101"),sQuery(id+"F4.wireOp",EDGE,"E102"),sQuery(id+"F4.wireOp",EDGE,"E103")])],"isStart":true});
            chamfer(context, id + "F16", {"entities" : qUnion([Q0]), "width" : 0.2 * mm});
        }
    });
